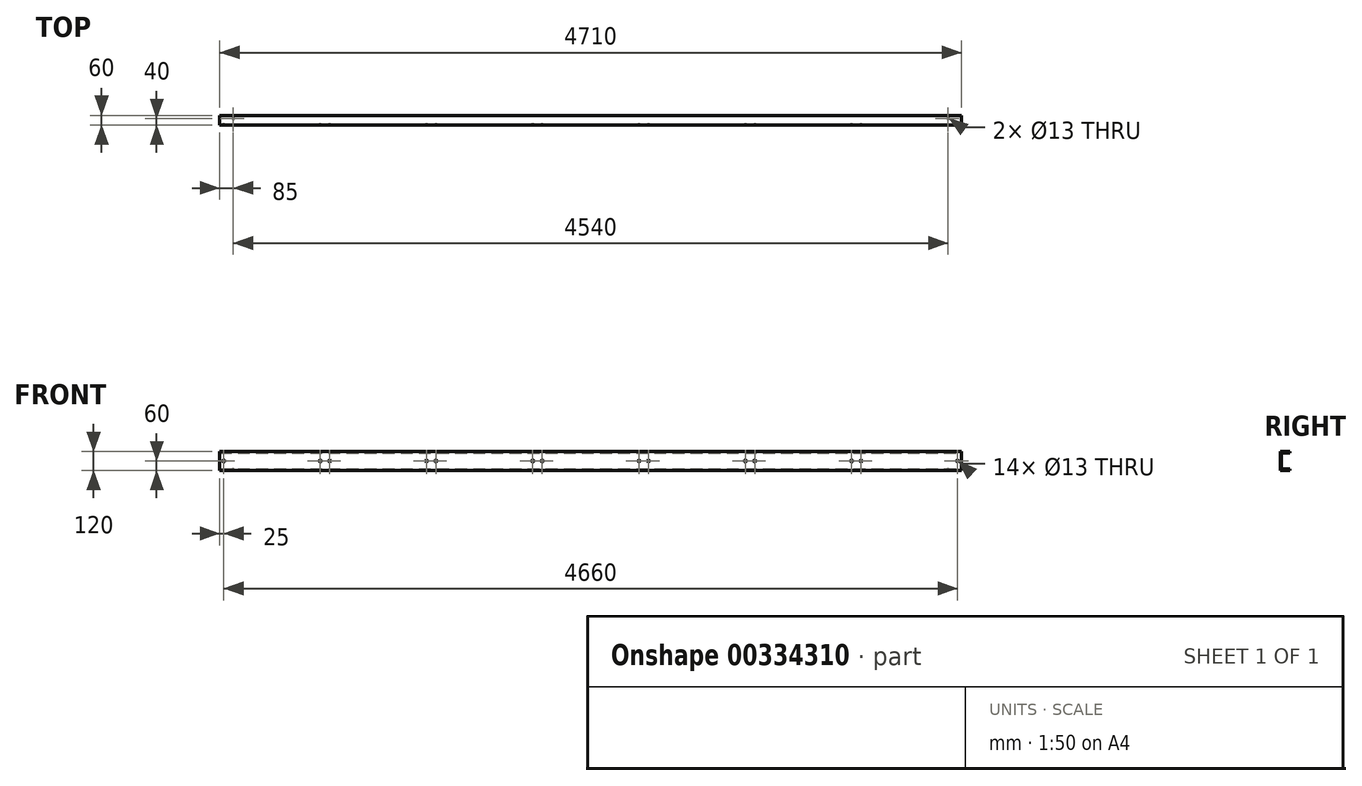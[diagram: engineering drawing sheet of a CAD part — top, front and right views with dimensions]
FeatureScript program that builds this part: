
annotation { "Feature Type Name" : "Feature", "Feature Type Description" : "" }
export const myFeature = defineFeature(function(context is Context, id is Id, definition is map)
    precondition{}
    {
        {
            assignVariable(context, id + "F0", {"name" : "L_Pro", "anyValue" : 4710});
        }
        {
            assignVariable(context, id + "F1", {"name" : "L_Hoe", "anyValue" : 120});
        }
        {
            var Q0;
            Q0=qCreatedBy(makeId("Right.planeOp"),FACE);
            var sketch = newSketch(context, id + "F2", { "sketchPlane" : qUnion([Q0])});
            skLineSegment(sketch, "E0", {"start": v(0, 0) * mm, "end": v(-60, 0) * mm});
            skLineSegment(sketch, "E1", {"start": v(-60, 0) * mm, "end": v(-60, 120) * mm});
            skLineSegment(sketch, "E2", {"start": v(-60, 120) * mm, "end": v(0, 120) * mm});
            skLineSegment(sketch, "E3", {"start": v(0, 120) * mm, "end": v(0, 112) * mm});
            skLineSegment(sketch, "E4", {"start": v(0, 112) * mm, "end": v(-43, 112) * mm});
            skLineSegment(sketch, "E5", {"start": v(-55, 100) * mm, "end": v(-55, 20) * mm});
            skLineSegment(sketch, "E6", {"start": v(-43, 8) * mm, "end": v(0, 8) * mm});
            skLineSegment(sketch, "E7", {"start": v(0, 8) * mm, "end": v(0, 0) * mm});
            skPoint(sketch, "E8.visualSharp", {"position": v(-55, 112) * mm});
            skArc(sketch, "E8.filletArc", {"start": v(-43, 112) * mm, "mid": v(-51.49, 108.49) * mm, "end": v(-55, 100) * mm});
            skPoint(sketch, "E9.visualSharp", {"position": v(-55, 8) * mm});
            skArc(sketch, "E9.filletArc", {"start": v(-55, 20) * mm, "mid": v(-51.49, 11.51) * mm, "end": v(-43, 8) * mm});
            skSolve(sketch);
        }
        {
            var Q0;
            Q0=qSketchRegion(id+"F2",true);
            var Q1;
            Q1=qConstructionFilter(qBodyType(qCreatedBy(id+"F2",EDGE),BodyType.WIRE),ConstructionObject.NO);
            extrude(context, id + "F3", {"entities" : qUnion([Q0]), "surfaceEntities" : qUnion([Q1]), "oppositeDirection" : true, "depth" : (getVariable(context, 'L_Pro')) * mm});
        }
        {
            var Q0;
            Q0=makeQuery(id+"F3.opExtrude","SWEPT_FACE",FACE,{"disambiguationData":[OSD([sQuery(id+"F2.wireOp",EDGE,"E6")])]});
            var sketch = newSketch(context, id + "F4", { "sketchPlane" : qUnion([Q0])});
            skCircle(sketch, "E10", {"center": v(-85, -20) * mm, "radius": 6.5 * mm});
            skCircle(sketch, "E11", {"center": v(-265, -20) * mm, "radius": 6.5 * mm, "construction": true});
            skCircle(sketch, "E12", {"center": v(-4625, -20) * mm, "radius": 6.5 * mm});
            skCircle(sketch, "E13", {"center": v(-4445, -20) * mm, "radius": 6.5 * mm, "construction": true});
            skSolve(sketch);
        }
        {
            var Q0;
            Q0=makeQuery(id+"F4.imprint","IMPRINT",FACE,{"disambiguationData":[TD([[makeQuery(id+"F4.imprint","IMPRINT",EDGE,{"derivedFrom":sQuery(id+"F4.wireOp",EDGE,"E12")}),1.0]])]});
            var Q1;
            Q1=makeQuery(id+"F4.imprint","IMPRINT",FACE,{"disambiguationData":[TD([[makeQuery(id+"F4.imprint","IMPRINT",EDGE,{"derivedFrom":sQuery(id+"F4.wireOp",EDGE,"E13")}),1.0]])]});
            var Q2;
            Q2=makeQuery(id+"F4.imprint","IMPRINT",FACE,{"disambiguationData":[TD([[makeQuery(id+"F4.imprint","IMPRINT",EDGE,{"derivedFrom":sQuery(id+"F4.wireOp",EDGE,"E10")}),1.0]])]});
            extrude(context, id + "F5", {"entities" : qUnion([Q0, Q1, Q2]), "operationType" : NewBodyOperationType.REMOVE, "endBound" : BoundingType.UP_TO_NEXT, "oppositeDirection" : true, "depth" : (2 * getVariable(context, 'L_Hoe')) * mm});
        }
        {
            var Q0;
            Q0=makeQuery(id+"F3.opExtrude","SWEPT_FACE",FACE,{"disambiguationData":[OSD([sQuery(id+"F2.wireOp",EDGE,"E1")])]});
            var sketch = newSketch(context, id + "F6", { "sketchPlane" : qUnion([Q0])});
            skLineSegment(sketch, "E14", {"start": v(-2355, 120) * mm, "end": v(-2355, 0) * mm, "construction": true});
            skCircle(sketch, "E15", {"center": v(-2047.5, 60) * mm, "radius": 6.5 * mm});
            skPoint(sketch, "E15.centerSnap0", {"position": v(0, 60) * mm});
            skCircle(sketch, "E16", {"center": v(-1987.5, 60) * mm, "radius": 6.5 * mm});
            skCircle(sketch, "E17", {"center": v(-1372.5, 60) * mm, "radius": 6.5 * mm});
            skCircle(sketch, "E18", {"center": v(-1312.5, 60) * mm, "radius": 6.5 * mm});
            skCircle(sketch, "E19", {"center": v(-697.5, 60) * mm, "radius": 6.5 * mm});
            skCircle(sketch, "E20", {"center": v(-637.5, 60) * mm, "radius": 6.5 * mm});
            skCircle(sketch, "E21", {"center": v(-25, 60) * mm, "radius": 6.5 * mm});
            skCircle(sketch, "E22.MirrorC", {"center": v(-2662.5, 60) * mm, "radius": 6.5 * mm});
            skCircle(sketch, "E23.MirrorC", {"center": v(-2722.5, 60) * mm, "radius": 6.5 * mm});
            skCircle(sketch, "E24.MirrorC", {"center": v(-3337.5, 60) * mm, "radius": 6.5 * mm});
            skCircle(sketch, "E25.MirrorC", {"center": v(-3397.5, 60) * mm, "radius": 6.5 * mm});
            skCircle(sketch, "E26.MirrorC", {"center": v(-4012.5, 60) * mm, "radius": 6.5 * mm});
            skCircle(sketch, "E27.MirrorC", {"center": v(-4072.5, 60) * mm, "radius": 6.5 * mm});
            skCircle(sketch, "E28.MirrorC", {"center": v(-4685, 60) * mm, "radius": 6.5 * mm});
            skSolve(sketch);
        }
        {
            var Q0;
            Q0=qSketchRegion(id+"F6",true);
            extrude(context, id + "F7", {"entities" : qUnion([Q0]), "operationType" : NewBodyOperationType.REMOVE, "endBound" : BoundingType.THROUGH_ALL, "oppositeDirection" : true, "depth" : 25 * mm});
        }
    });
